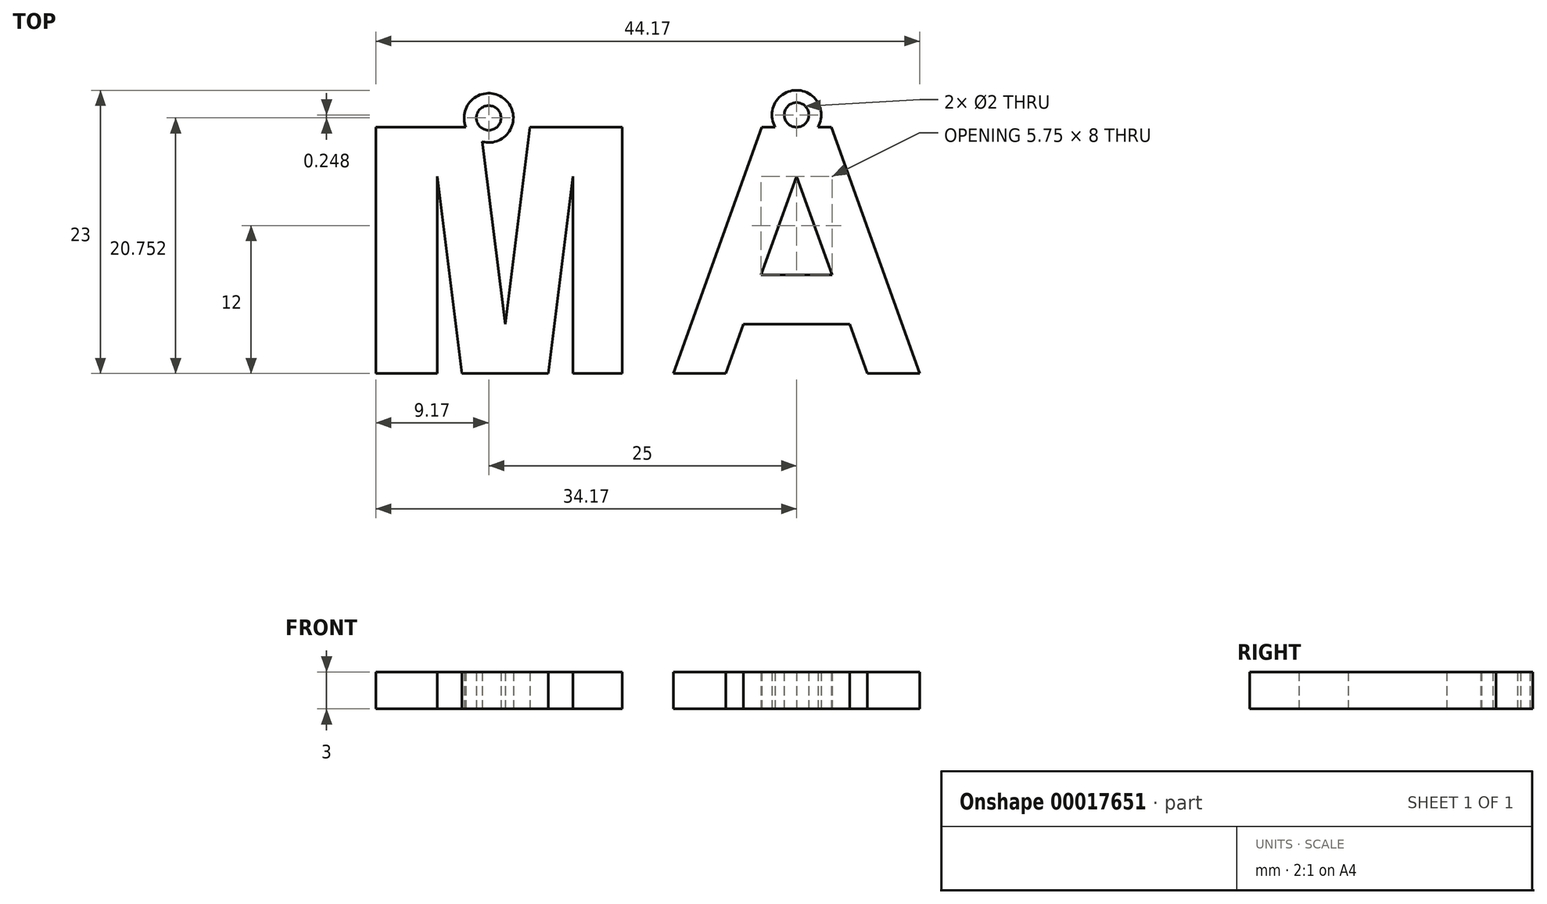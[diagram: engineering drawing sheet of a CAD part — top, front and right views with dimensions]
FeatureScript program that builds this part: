
annotation { "Feature Type Name" : "Feature", "Feature Type Description" : "" }
export const myFeature = defineFeature(function(context is Context, id is Id, definition is map)
    precondition{}
    {
        {
            var Q0;
            Q0=qCreatedBy(makeId("Top.planeOp"),FACE);
            var sketch = newSketch(context, id + "F0", { "sketchPlane" : qUnion([Q0])});
            skLineSegment(sketch, "E0", {"start": v(-4.17, -4) * mm, "end": v(-4.17, -20) * mm});
            skLineSegment(sketch, "E1", {"start": v(-4.17, -20) * mm, "end": v(-9.17, -20) * mm});
            skLineSegment(sketch, "E2", {"start": v(-9.17, -20) * mm, "end": v(-9.17, 0) * mm});
            skLineSegment(sketch, "E3", {"start": v(-9.17, 0) * mm, "end": v(-0.66, 0) * mm});
            skLineSegment(sketch, "E4", {"start": v(-0.66, 0) * mm, "end": v(1.34, -16) * mm});
            skLineSegment(sketch, "E5", {"start": v(1.34, -16) * mm, "end": v(3.34, 0) * mm});
            skLineSegment(sketch, "E6", {"start": v(3.34, 0) * mm, "end": v(10.83, 0) * mm});
            skLineSegment(sketch, "E7", {"start": v(10.83, 0) * mm, "end": v(10.83, -20) * mm});
            skLineSegment(sketch, "E8", {"start": v(10.83, -20) * mm, "end": v(6.85, -20) * mm});
            skLineSegment(sketch, "E9", {"start": v(6.85, -20) * mm, "end": v(6.85, -4) * mm});
            skLineSegment(sketch, "E10", {"start": v(6.85, -4) * mm, "end": v(4.85, -20) * mm});
            skLineSegment(sketch, "E11", {"start": v(4.85, -20) * mm, "end": v(-2.17, -20) * mm});
            skLineSegment(sketch, "E12", {"start": v(-2.17, -20) * mm, "end": v(-4.17, -4) * mm});
            skLineSegment(sketch, "E13", {"start": v(-0.66, 0) * mm, "end": v(3.34, 0) * mm, "construction": true});
            skLineSegment(sketch, "E14", {"start": v(-4.17, -20) * mm, "end": v(-2.17, -20) * mm, "construction": true});
            skLineSegment(sketch, "E15", {"start": v(6.85, -20) * mm, "end": v(4.85, -20) * mm, "construction": true});
            skLineSegment(sketch, "E16", {"start": v(-4.17, -4) * mm, "end": v(-0.22, -3.5) * mm, "construction": true});
            skLineSegment(sketch, "E17", {"start": v(6.85, -4) * mm, "end": v(2.9, -3.5) * mm, "construction": true});
            skCircle(sketch, "E18", {"center": v(0, 0.75) * mm, "radius": 1 * mm});
            skCircle(sketch, "E19", {"center": v(0, 0.75) * mm, "radius": 2 * mm});
            skLineSegment(sketch, "E20", {"start": v(0, 0.75) * mm, "end": v(-4.17, -4) * mm, "construction": true});
            skSolve(sketch);
        }
        {
            var Q0;
            Q0 = qSketchRegion(id + "F0", true);
            extrude(context, id + "F1", {"entities" : qUnion([Q0]), "depth" : 3 * mm});
        }
        {
            var Q0;
            Q0=makeQuery(id+"F1.opExtrude","SWEPT_BODY",BODY,{"disambiguationData":[OSD([sQuery(id+"F0.wireOp",EDGE,"E0"),sQuery(id+"F0.wireOp",EDGE,"E1"),sQuery(id+"F0.wireOp",EDGE,"E2"),sQuery(id+"F0.wireOp",EDGE,"E3"),sQuery(id+"F0.wireOp",EDGE,"E4"),sQuery(id+"F0.wireOp",EDGE,"E5"),sQuery(id+"F0.wireOp",EDGE,"E6"),sQuery(id+"F0.wireOp",EDGE,"E7"),sQuery(id+"F0.wireOp",EDGE,"E8"),sQuery(id+"F0.wireOp",EDGE,"E9"),sQuery(id+"F0.wireOp",EDGE,"E10"),sQuery(id+"F0.wireOp",EDGE,"E11"),sQuery(id+"F0.wireOp",EDGE,"E12")])]});
            transform(context, id + "F2", {"entities" : qUnion([Q0]), "transformType" : TransformType.TRANSLATION_3D, "dx" : 50 * mm, "dy" : 50 * mm, "dz" : 0 * mm, "makeCopy" : false});
        }
        {
            var Q0;
            Q0=qCreatedBy(makeId("Top.planeOp"),FACE);
            var sketch = newSketch(context, id + "F3", { "sketchPlane" : qUnion([Q0])});
            skLineSegment(sketch, "E21", {"start": v(-2.87, -12) * mm, "end": v(0, -4) * mm});
            skLineSegment(sketch, "E22", {"start": v(0, -4) * mm, "end": v(2.87, -12) * mm});
            skLineSegment(sketch, "E23", {"start": v(2.87, -12) * mm, "end": v(-2.87, -12) * mm});
            skLineSegment(sketch, "E24", {"start": v(-2.81, 0) * mm, "end": v(2.81, 0) * mm});
            skLineSegment(sketch, "E25", {"start": v(2.81, 0) * mm, "end": v(10, -20) * mm});
            skLineSegment(sketch, "E26", {"start": v(10, -20) * mm, "end": v(5.75, -20) * mm});
            skLineSegment(sketch, "E27", {"start": v(5.75, -20) * mm, "end": v(4.31, -16) * mm});
            skLineSegment(sketch, "E28", {"start": v(4.31, -16) * mm, "end": v(-4.31, -16) * mm});
            skLineSegment(sketch, "E29", {"start": v(-4.31, -16) * mm, "end": v(-5.75, -20) * mm});
            skLineSegment(sketch, "E30", {"start": v(-5.75, -20) * mm, "end": v(-10, -20) * mm});
            skLineSegment(sketch, "E31", {"start": v(-10, -20) * mm, "end": v(-2.81, 0) * mm});
            skLineSegment(sketch, "E32", {"start": v(0, -4) * mm, "end": v(3.76, -2.65) * mm, "construction": true});
            skLineSegment(sketch, "E33", {"start": v(4.31, -16) * mm, "end": v(8.08, -14.65) * mm, "construction": true});
            skLineSegment(sketch, "E34", {"start": v(-2.87, -12) * mm, "end": v(-2.87, -16) * mm, "construction": true});
            skCircle(sketch, "E35", {"center": v(0, 1) * mm, "radius": 1 * mm});
            skCircle(sketch, "E36", {"center": v(0, 1) * mm, "radius": 2 * mm});
            skLineSegment(sketch, "E37", {"start": v(0, -4) * mm, "end": v(0, 0) * mm, "construction": true});
            skLineSegment(sketch, "E38", {"start": v(-4.31, -16) * mm, "end": v(-4.31, -20) * mm, "construction": true});
            skLineSegment(sketch, "E39", {"start": v(0, -4) * mm, "end": v(-3.76, -2.65) * mm, "construction": true});
            skSolve(sketch);
        }
        {
            var Q0;
            Q0 = qSketchRegion(id + "F3", true);
            extrude(context, id + "F4", {"entities" : qUnion([Q0]), "depth" : 3 * mm});
        }
        {
            var Q0;
            Q0=makeQuery(id+"F4.opExtrude","SWEPT_BODY",BODY,{"disambiguationData":[OSD([sQuery(id+"F3.wireOp",EDGE,"E21"),sQuery(id+"F3.wireOp",EDGE,"E22"),sQuery(id+"F3.wireOp",EDGE,"E23"),sQuery(id+"F3.wireOp",EDGE,"E24"),sQuery(id+"F3.wireOp",EDGE,"E25"),sQuery(id+"F3.wireOp",EDGE,"E26"),sQuery(id+"F3.wireOp",EDGE,"E27"),sQuery(id+"F3.wireOp",EDGE,"E28"),sQuery(id+"F3.wireOp",EDGE,"E29"),sQuery(id+"F3.wireOp",EDGE,"E30"),sQuery(id+"F3.wireOp",EDGE,"E31"),sQuery(id+"F3.wireOp",EDGE,"E35"),sQuery(id+"F3.wireOp",EDGE,"E36")])]});
            transform(context, id + "F5", {"entities" : qUnion([Q0]), "transformType" : TransformType.TRANSLATION_3D, "dx" : 75 * mm, "dy" : 50 * mm, "dz" : 0 * mm, "makeCopy" : false});
        }
    });
